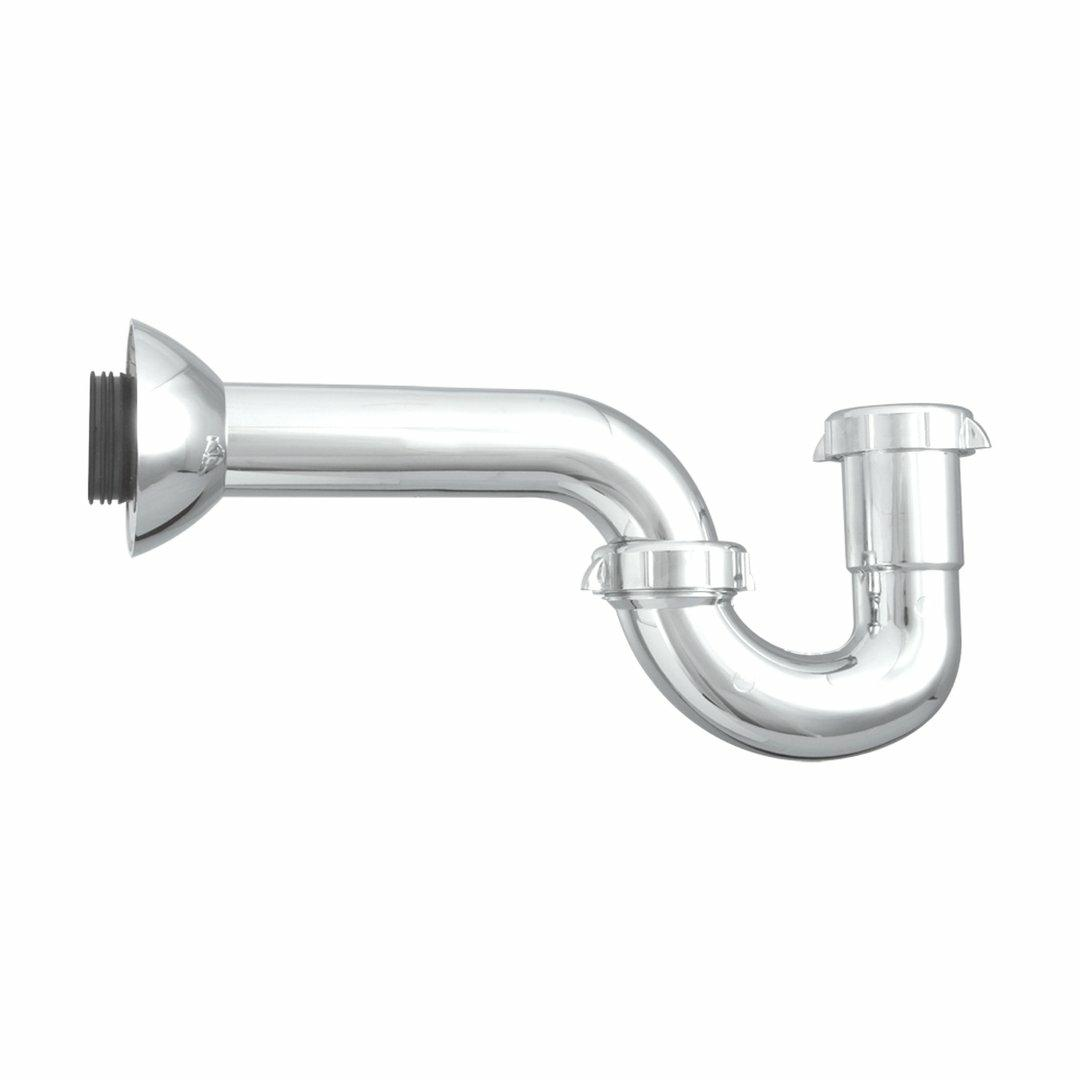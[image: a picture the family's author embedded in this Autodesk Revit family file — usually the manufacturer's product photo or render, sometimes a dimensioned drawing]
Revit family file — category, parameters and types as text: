
# Revit family: BIM_L1-3008-11
name_source: partatom
category: Aparatos sanitarios
units: mm (PartAtom-declared; Revit-internal decimal feet)

## family parameters
Activar corte en vistas = No
Anfitrión = Cara
Compartido = No
Corte con vacíos al cargar = No
Cota de conector redondo = Usar diámetro
Mantener orientación de anotación = No
Número OmniClass = 23.31.11.00
Punto de cálculo de habitación = No
Tipo de pieza = Normal

## types (1)
- L1-3008-11
    Acabado = Cepillado Brillante
    Alto = 160 mm  [stored 0.524934 ft]
    Ancho = 600 mm
    Conexión AC = Sí
    Conexión AF = Sí
    Conexión de residuos = No
    Conexión de ventilación = No
    Date Modified = 08-08-2025
    Descripción = Lavaplatos en acero
    Elevación por defecto = 0 mm  [stored 0 ft]
    Fabricante = Gricol
    Garantia Especifica = 5 años
    Imagen de tipo = FOTO LAVAPLATOS EN ACERO POCETA 60x40 cm.JPG
    Largo = 400 mm
    Link Ficha Tecnica = https://infotecnica.gricol.com
    Material = Acero inoxidable
    Materiales del producto = Acero Inoxidable
    Modelo = L1-3008-11
    Peso = 2.50 kg
    Product Name = Lavaplatos De Empotrar 60 X 40 Cm Con Complementos
    Resistencia a Corrosión = Si
    Tipo de Uso = Residencial
    URL = https://www.gricol.com

note: [stored X ft] marks values corroborated as IEEE doubles in the binary element streams (Revit-internal decimal feet)

## geometry (parser evidence)
native form markers: Blend x8, Sweep x14
no freeform markers — native parametric forms only
